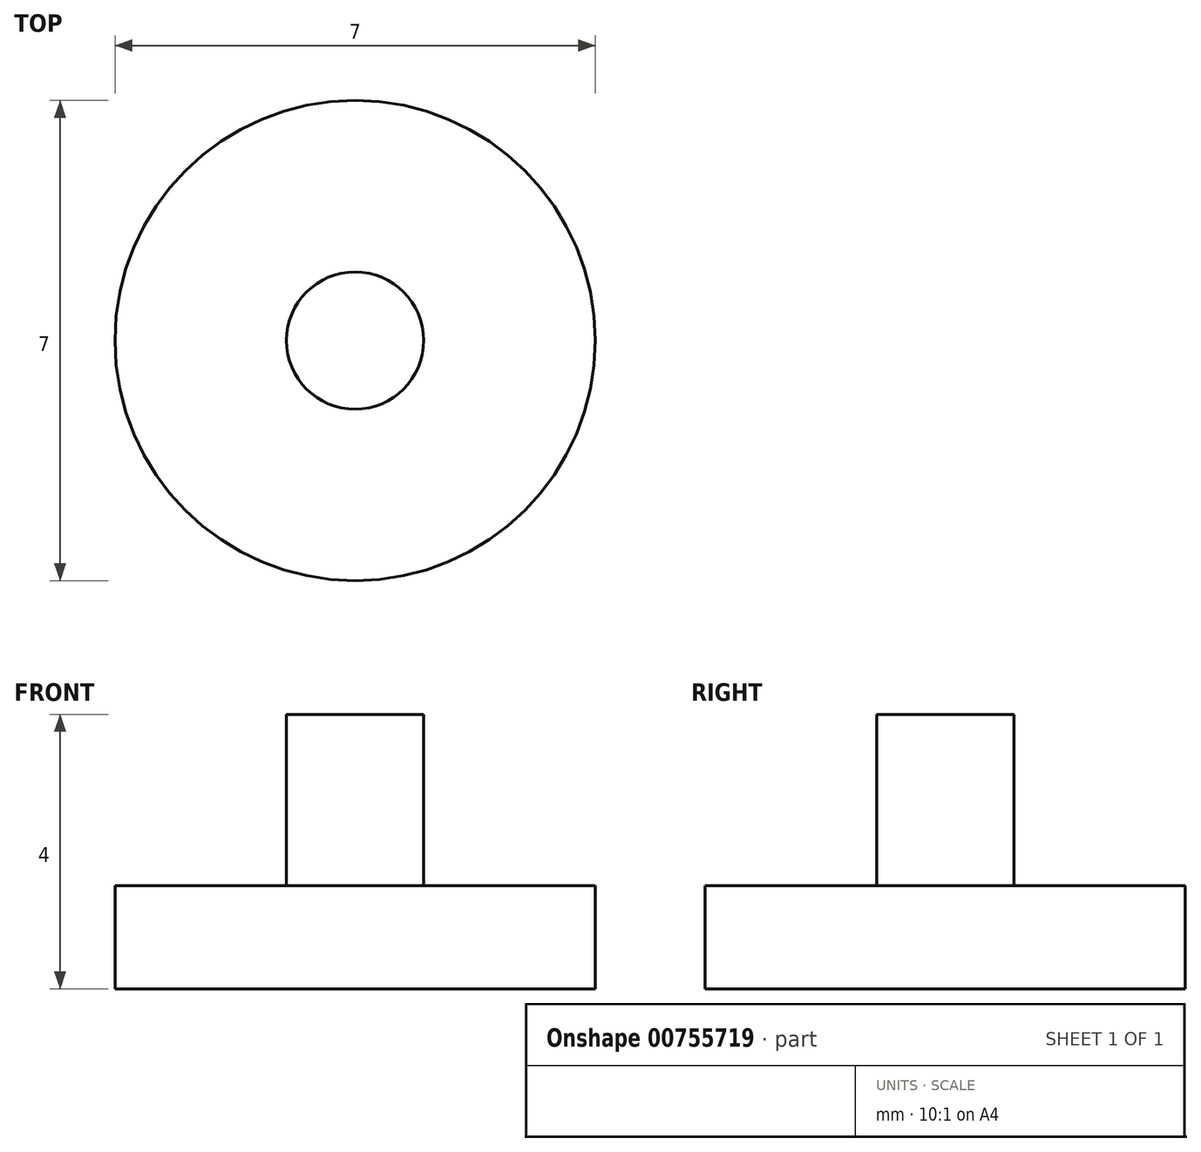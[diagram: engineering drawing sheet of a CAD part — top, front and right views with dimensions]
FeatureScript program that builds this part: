
annotation { "Feature Type Name" : "Feature", "Feature Type Description" : "" }
export const myFeature = defineFeature(function(context is Context, id is Id, definition is map)
    precondition{}
    {
        {
            var Q0;
            Q0=qCreatedBy(makeId("Top.planeOp"),FACE);
            var sketch = newSketch(context, id + "F0", { "sketchPlane" : qUnion([Q0])});
            skCircle(sketch, "E0", {"center": v(0, 0) * mm, "radius": 3.5 * mm});
            skCircle(sketch, "E1", {"center": v(0, 0) * mm, "radius": 1 * mm});
            skSolve(sketch);
        }
        {
            var Q0;
            Q0=makeQuery(id+"F0.imprint","IMPRINT",FACE,{"disambiguationData":[TD([[makeQuery(id+"F0.imprint","IMPRINT",EDGE,{"derivedFrom":sQuery(id+"F0.wireOp",EDGE,"E1")}),1.0]])]});
            var Q1;
            Q1=sQuery(id+"F0.wireOp",EDGE,"E1");
            extrude(context, id + "F1", {"entities" : qUnion([Q0]), "surfaceEntities" : qUnion([Q1]), "depth" : 4 * mm, "offsetDistance" : 25 * mm});
        }
        {
            var Q0;
            Q0 = qSketchRegion(id + "F0", true);
            extrude(context, id + "F2", {"entities" : qUnion([Q0]), "operationType" : NewBodyOperationType.ADD, "depth" : 1.5 * mm, "offsetDistance" : 25 * mm});
        }
    });
